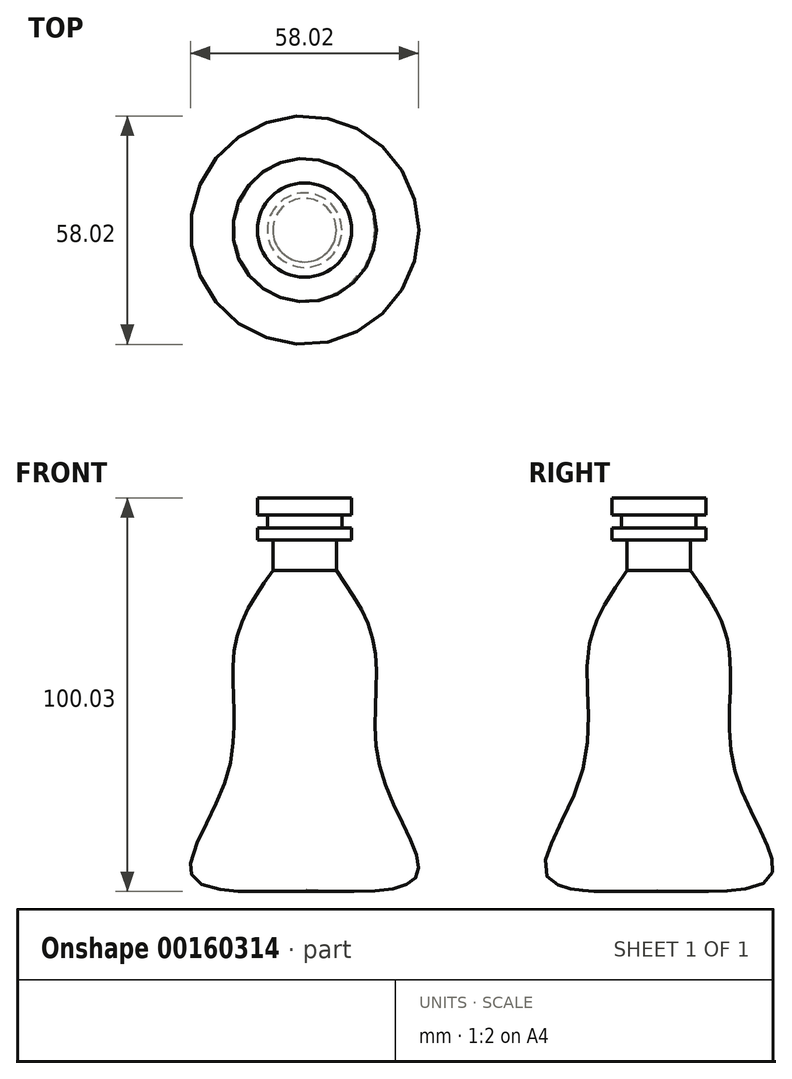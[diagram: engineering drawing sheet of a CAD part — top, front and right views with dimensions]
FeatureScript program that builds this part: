
annotation { "Feature Type Name" : "Feature", "Feature Type Description" : "" }
export const myFeature = defineFeature(function(context is Context, id is Id, definition is map)
    precondition{}
    {
        {
            var Q0;
            Q0=qCreatedBy(makeId("Front.planeOp"),FACE);
            var sketch = newSketch(context, id + "F0", { "sketchPlane" : qUnion([Q0])});
            skLineSegment(sketch, "E0", {"start": v(0, 0) * mm, "end": v(0, 59.42) * mm});
            skLineSegment(sketch, "E1", {"start": v(0, 0) * mm, "end": v(0, -63.03) * mm});
            skLineSegment(sketch, "E2", {"start": v(0, 59.42) * mm, "end": v(11.97, 59.42) * mm});
            skLineSegment(sketch, "E3", {"start": v(11.97, 59.42) * mm, "end": v(11.97, 55.1) * mm});
            skLineSegment(sketch, "E4", {"start": v(11.97, 55.1) * mm, "end": v(9.46, 55.1) * mm});
            skLineSegment(sketch, "E5", {"start": v(9.46, 55.1) * mm, "end": v(9.46, 51.76) * mm});
            skLineSegment(sketch, "E6", {"start": v(9.46, 51.76) * mm, "end": v(11.97, 51.76) * mm});
            skLineSegment(sketch, "E7", {"start": v(11.97, 51.76) * mm, "end": v(11.97, 48.7) * mm});
            skLineSegment(sketch, "E8", {"start": v(11.97, 48.7) * mm, "end": v(8.07, 48.7) * mm});
            skLineSegment(sketch, "E9", {"start": v(8.07, 48.7) * mm, "end": v(8.07, 40.9) * mm});
            skFitSpline(sketch, "E10", {"points": [v(8.07, 40.9) * mm, v(17.81, 21.29) * mm, v(19.48, -10.44) * mm, v(28.66, -36.32) * mm, v(0, -40.21) * mm], "startDerivative": vector(57.27, -80.88) * mm, "endDerivative": vector(-154.54, 7.12) * mm});
            skSolve(sketch);
        }
        {
            var Q0;
            {var subQ0=sQuery(id+"F0.wireOp",EDGE,"E0");Q0=makeQuery(id+"F0.imprint","IMPRINT",FACE,{"disambiguationData":[TD([[makeQuery(id+"F0.imprint","IMPRINT",EDGE,{"derivedFrom":subQ0}),-1.0]])]});}
            var Q1;
            Q1=sQuery(id+"F0.wireOp",EDGE,"E0");
            revolve(context, id + "F1", {"entities" : qUnion([Q0]), "axis" : qUnion([Q1]), "revolveType" : RevolveType.FULL});
        }
    });
